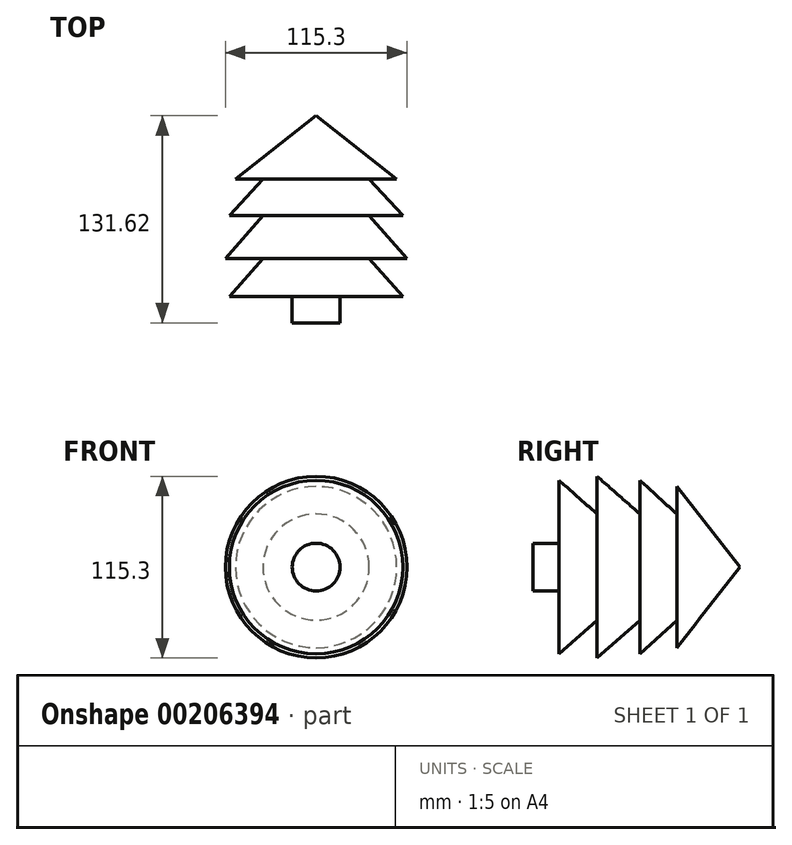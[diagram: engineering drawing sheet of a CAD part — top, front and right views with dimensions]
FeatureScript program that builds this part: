
annotation { "Feature Type Name" : "Feature", "Feature Type Description" : "" }
export const myFeature = defineFeature(function(context is Context, id is Id, definition is map)
    precondition{}
    {
        {
            var Q0;
            Q0=qCreatedBy(makeId("Top.planeOp"),FACE);
            var sketch = newSketch(context, id + "F0", { "sketchPlane" : qUnion([Q0])});
            skLineSegment(sketch, "E0", {"start": v(0, -54.98) * mm, "end": v(15.19, -54.98) * mm});
            skLineSegment(sketch, "E1", {"start": v(15.19, -54.98) * mm, "end": v(15.19, -38.39) * mm});
            skLineSegment(sketch, "E2", {"start": v(15.19, -38.39) * mm, "end": v(55.12, -38.39) * mm});
            skLineSegment(sketch, "E3", {"start": v(55.12, -38.39) * mm, "end": v(33.75, -14.2) * mm});
            skLineSegment(sketch, "E4", {"start": v(33.75, -14.2) * mm, "end": v(57.65, -14.2) * mm});
            skLineSegment(sketch, "E5", {"start": v(57.65, -14.2) * mm, "end": v(33.75, 13.08) * mm});
            skLineSegment(sketch, "E6", {"start": v(33.75, 13.08) * mm, "end": v(55.12, 13.08) * mm});
            skLineSegment(sketch, "E7", {"start": v(55.12, 13.08) * mm, "end": v(33.75, 36.42) * mm});
            skLineSegment(sketch, "E8", {"start": v(33.75, 36.42) * mm, "end": v(51.18, 36.42) * mm});
            skLineSegment(sketch, "E9", {"start": v(51.18, 36.42) * mm, "end": v(0, 76.64) * mm});
            skLineSegment(sketch, "E10", {"start": v(0, 76.64) * mm, "end": v(0, -54.98) * mm});
            skSolve(sketch);
        }
        {
            var Q0;
            Q0=makeQuery(id+"F0.imprint","IMPRINT",FACE,{"disambiguationData":[TD([[makeQuery(id+"F0.imprint","IMPRINT",EDGE,{"derivedFrom":sQuery(id+"F0.wireOp",EDGE,"E0")}),1.0]])]});
            var Q1;
            Q1=sQuery(id+"F0.wireOp",EDGE,"E10");
            revolve(context, id + "F1", {"entities" : qUnion([Q0]), "axis" : qUnion([Q1]), "revolveType" : RevolveType.FULL});
        }
    });
